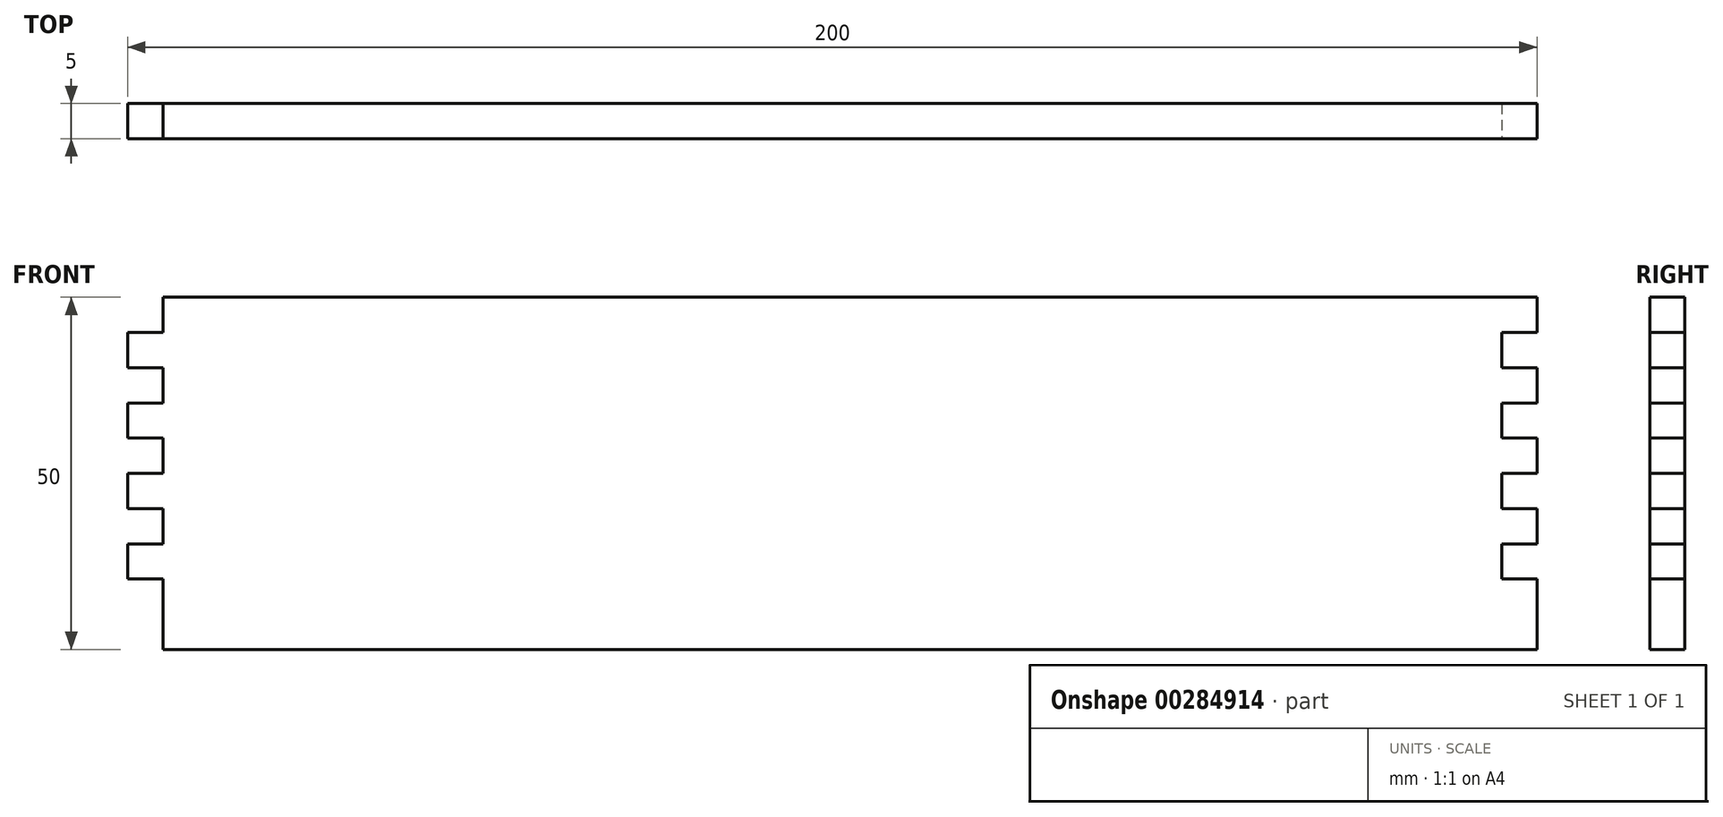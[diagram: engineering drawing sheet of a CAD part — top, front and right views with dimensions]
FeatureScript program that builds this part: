
annotation { "Feature Type Name" : "Feature", "Feature Type Description" : "" }
export const myFeature = defineFeature(function(context is Context, id is Id, definition is map)
    precondition{}
    {
        {
            var Q0;
            Q0=qCreatedBy(makeId("Front.planeOp"),FACE);
            var sketch = newSketch(context, id + "F0", { "sketchPlane" : qUnion([Q0])});
            skLineSegment(sketch, "E0", {"start": v(0, 25.02) * mm, "end": v(100, 25.02) * mm});
            skLineSegment(sketch, "E1", {"start": v(100, 25.02) * mm, "end": v(100, 20.02) * mm});
            skLineSegment(sketch, "E2", {"start": v(100, -24.98) * mm, "end": v(0, -24.98) * mm});
            skLineSegment(sketch, "E3.0", {"start": v(95, 20.02) * mm, "end": v(100, 20.02) * mm});
            skLineSegment(sketch, "E4.0", {"start": v(95, 15.02) * mm, "end": v(100, 15.02) * mm});
            skLineSegment(sketch, "E5.0", {"start": v(95, 10.02) * mm, "end": v(100, 10.02) * mm});
            skLineSegment(sketch, "E6.0.1.0", {"start": v(95, 0.02) * mm, "end": v(100, 0.02) * mm});
            skLineSegment(sketch, "E6.0.2.0", {"start": v(95, -4.98) * mm, "end": v(100, -4.98) * mm});
            skLineSegment(sketch, "E6.0.3.0", {"start": v(95, -9.98) * mm, "end": v(100, -9.98) * mm});
            skLineSegment(sketch, "E6.0.4.0", {"start": v(95, -14.98) * mm, "end": v(100, -14.98) * mm});
            skLineSegment(sketch, "E6.direction2", {"start": v(0, 5.02) * mm, "end": v(0, 0.02) * mm, "construction": true});
            skLineSegment(sketch, "E7.0", {"start": v(95, 20.02) * mm, "end": v(95, 15.02) * mm});
            skLineSegment(sketch, "E8.trimOffspring", {"start": v(100, 15.02) * mm, "end": v(100, 10.02) * mm});
            skLineSegment(sketch, "E9.trimOffspring", {"start": v(100, 5.02) * mm, "end": v(100, 0.02) * mm});
            skLineSegment(sketch, "E10.trimOffspring", {"start": v(100, -4.98) * mm, "end": v(100, -9.98) * mm});
            skLineSegment(sketch, "E11.trimOffspring", {"start": v(100, -14.98) * mm, "end": v(100, -24.98) * mm});
            skLineSegment(sketch, "E12.trimOffspring", {"start": v(95, 10.02) * mm, "end": v(95, 5.02) * mm});
            skLineSegment(sketch, "E13.trimOffspring", {"start": v(95, 0.02) * mm, "end": v(95, -4.98) * mm});
            skLineSegment(sketch, "E14.trimOffspring", {"start": v(95, -9.98) * mm, "end": v(95, -14.98) * mm});
            skLineSegment(sketch, "E15.trimOffspring", {"start": v(95, 5.02) * mm, "end": v(100, 5.02) * mm});
            skPoint(sketch, "E16.orphan", {"position": v(0, -4.98) * mm});
            skPoint(sketch, "E17.orphan", {"position": v(0, -9.98) * mm});
            skPoint(sketch, "E18.orphan", {"position": v(0, -14.98) * mm});
            skLineSegment(sketch, "E19.MirrorCS", {"start": v(-95, -24.98) * mm, "end": v(0, -24.98) * mm});
            skLineSegment(sketch, "E20.MirrorCS", {"start": v(-95, -9.98) * mm, "end": v(-100, -9.98) * mm});
            skLineSegment(sketch, "E21.MirrorCS", {"start": v(-95, 0.02) * mm, "end": v(-100, 0.02) * mm});
            skLineSegment(sketch, "E22.MirrorCS", {"start": v(-95, 20.02) * mm, "end": v(-100, 20.02) * mm});
            skLineSegment(sketch, "E23.MirrorCS", {"start": v(-95, 5.02) * mm, "end": v(-100, 5.02) * mm});
            skLineSegment(sketch, "E24.MirrorCS", {"start": v(-95, -14.98) * mm, "end": v(-100, -14.98) * mm});
            skLineSegment(sketch, "E25.MirrorCS", {"start": v(0, 25.02) * mm, "end": v(-95, 25.02) * mm});
            skLineSegment(sketch, "E26.MirrorCS", {"start": v(-95, 15.02) * mm, "end": v(-100, 15.02) * mm});
            skLineSegment(sketch, "E27.MirrorCS", {"start": v(-95, 10.02) * mm, "end": v(-100, 10.02) * mm});
            skLineSegment(sketch, "E28.MirrorCS", {"start": v(-95, -4.98) * mm, "end": v(-100, -4.98) * mm});
            skLineSegment(sketch, "E29", {"start": v(-100, 20.02) * mm, "end": v(-100, 15.02) * mm});
            skLineSegment(sketch, "E30", {"start": v(-100, 10.02) * mm, "end": v(-100, 5.02) * mm});
            skLineSegment(sketch, "E31", {"start": v(-100, 0.02) * mm, "end": v(-100, -4.98) * mm});
            skLineSegment(sketch, "E32", {"start": v(-100, -9.98) * mm, "end": v(-100, -14.98) * mm});
            skLineSegment(sketch, "E33", {"start": v(-95, -14.98) * mm, "end": v(-95, -24.98) * mm});
            skPoint(sketch, "E33.endSnap0", {"position": v(-95, -12.48) * mm});
            skLineSegment(sketch, "E34", {"start": v(-95, -4.98) * mm, "end": v(-95, -9.98) * mm});
            skLineSegment(sketch, "E35", {"start": v(-95, 5.02) * mm, "end": v(-95, 0.02) * mm});
            skLineSegment(sketch, "E36", {"start": v(-95, 15.02) * mm, "end": v(-95, 10.02) * mm});
            skLineSegment(sketch, "E37", {"start": v(-95, 20.02) * mm, "end": v(-95, 25.02) * mm});
            skPoint(sketch, "E38.orphan", {"position": v(-100, 25.02) * mm});
            skPoint(sketch, "E39.orphan", {"position": v(-100, -24.98) * mm});
            skSolve(sketch);
        }
        {
            var Q0;
            Q0 = qSketchRegion(id + "F0", true);
            extrude(context, id + "F1", {"entities" : qUnion([Q0]), "oppositeDirection" : true, "depth" : 5 * mm});
        }
    });
